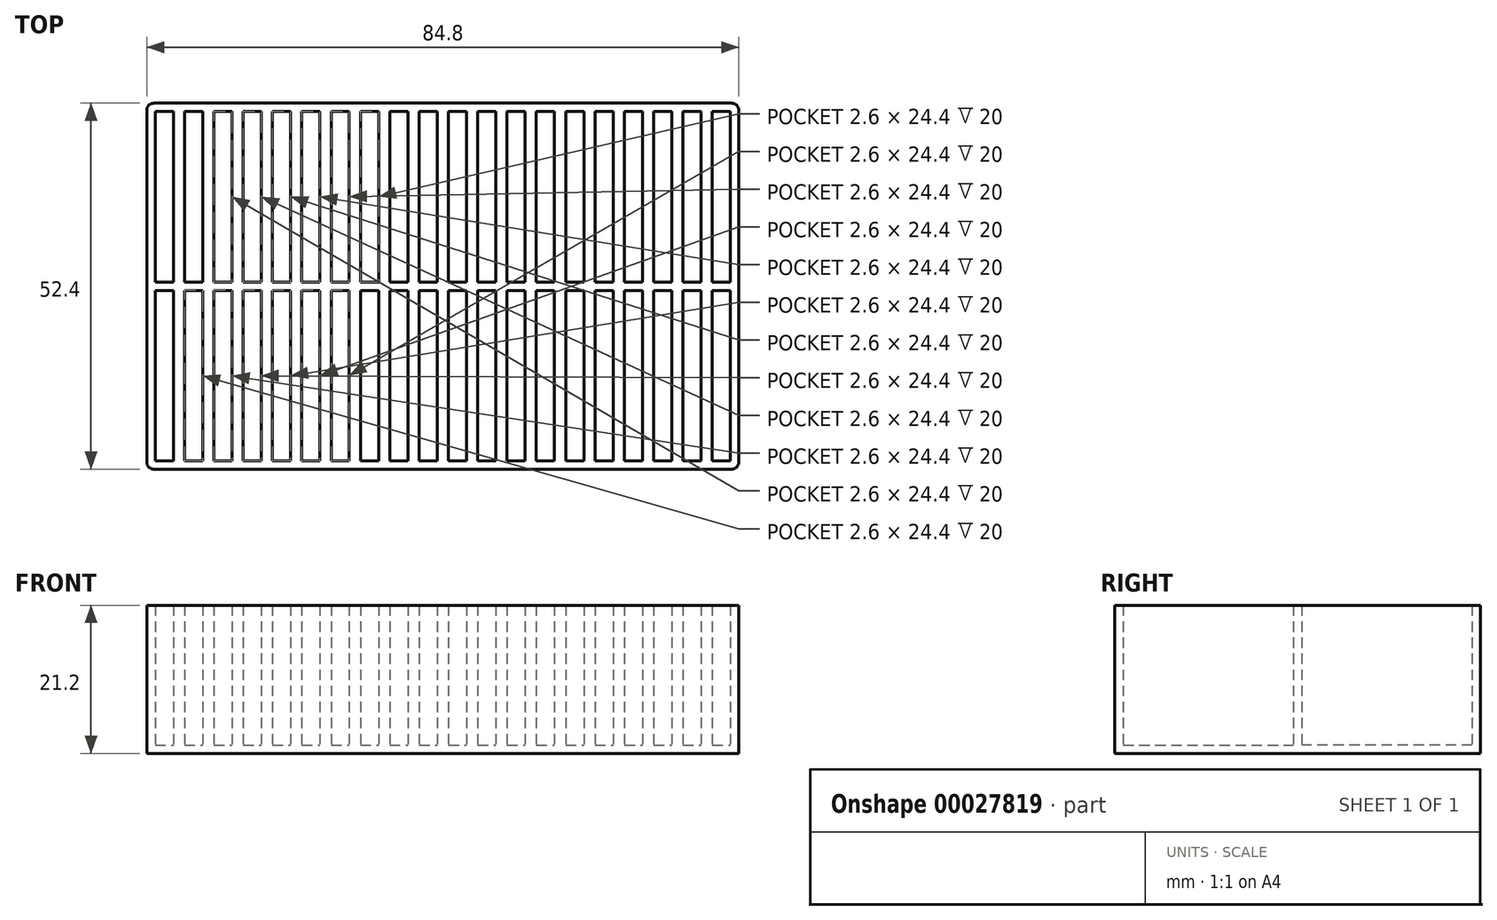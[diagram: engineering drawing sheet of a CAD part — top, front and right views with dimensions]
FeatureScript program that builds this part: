
annotation { "Feature Type Name" : "Feature", "Feature Type Description" : "" }
export const myFeature = defineFeature(function(context is Context, id is Id, definition is map)
    precondition{}
    {
        {
            var Q0;
            Q0=qCreatedBy(makeId("Top.planeOp"),FACE);
            var sketch = newSketch(context, id + "F0", { "sketchPlane" : qUnion([Q0])});
            skLineSegment(sketch, "E0.rect.bottom", {"start": v(-42.4, -26.2) * mm, "end": v(42.4, -26.2) * mm});
            skLineSegment(sketch, "E0.rect.top", {"start": v(-42.4, 26.2) * mm, "end": v(42.4, 26.2) * mm});
            skLineSegment(sketch, "E0.rect.left", {"start": v(-42.4, -26.2) * mm, "end": v(-42.4, 26.2) * mm});
            skLineSegment(sketch, "E0.rect.right", {"start": v(42.4, -26.2) * mm, "end": v(42.4, 26.2) * mm});
            skPoint(sketch, "E0.rect.middle", {"position": v(0, 0) * mm});
            skLineSegment(sketch, "E1", {"start": v(-42.4, 0) * mm, "end": v(42.4, 0) * mm, "construction": true});
            skLineSegment(sketch, "E2.bottom", {"start": v(-41.2, 25) * mm, "end": v(-38.6, 25) * mm});
            skLineSegment(sketch, "E2.top", {"start": v(-41.2, 0.6) * mm, "end": v(-38.6, 0.6) * mm});
            skLineSegment(sketch, "E2.left", {"start": v(-41.2, 25) * mm, "end": v(-41.2, 0.6) * mm});
            skLineSegment(sketch, "E2.right", {"start": v(-38.6, 25) * mm, "end": v(-38.6, 0.6) * mm});
            skLineSegment(sketch, "E3.0.MirrorCS", {"start": v(-38.6, -25) * mm, "end": v(-38.6, -0.6) * mm});
            skLineSegment(sketch, "E4.0.MirrorCS", {"start": v(-41.2, -0.6) * mm, "end": v(-38.6, -0.6) * mm});
            skLineSegment(sketch, "E5.0.MirrorCS", {"start": v(-41.2, -25) * mm, "end": v(-41.2, -0.6) * mm});
            skLineSegment(sketch, "E6.0.MirrorCS", {"start": v(-41.2, -25) * mm, "end": v(-38.6, -25) * mm});
            skLineSegment(sketch, "E7.1.0.0", {"start": v(-37, 25) * mm, "end": v(-37, 0.6) * mm});
            skLineSegment(sketch, "E7.1.0.1", {"start": v(-34.4, 25) * mm, "end": v(-34.4, 0.6) * mm});
            skLineSegment(sketch, "E7.1.0.2", {"start": v(-37, 25) * mm, "end": v(-34.4, 25) * mm});
            skLineSegment(sketch, "E7.1.0.3", {"start": v(-37, 0.6) * mm, "end": v(-34.4, 0.6) * mm});
            skLineSegment(sketch, "E7.1.0.4", {"start": v(-37, -0.6) * mm, "end": v(-34.4, -0.6) * mm});
            skLineSegment(sketch, "E7.1.0.5", {"start": v(-34.4, -25) * mm, "end": v(-34.4, -0.6) * mm});
            skLineSegment(sketch, "E7.1.0.6", {"start": v(-37, -25) * mm, "end": v(-34.4, -25) * mm});
            skLineSegment(sketch, "E7.1.0.7", {"start": v(-37, -25) * mm, "end": v(-37, -0.6) * mm});
            skLineSegment(sketch, "E7.2.0.0", {"start": v(-32.8, 25) * mm, "end": v(-32.8, 0.6) * mm});
            skLineSegment(sketch, "E7.2.0.1", {"start": v(-30.2, 25) * mm, "end": v(-30.2, 0.6) * mm});
            skLineSegment(sketch, "E7.2.0.2", {"start": v(-32.8, 25) * mm, "end": v(-30.2, 25) * mm});
            skLineSegment(sketch, "E7.2.0.3", {"start": v(-32.8, 0.6) * mm, "end": v(-30.2, 0.6) * mm});
            skLineSegment(sketch, "E7.2.0.4", {"start": v(-32.8, -0.6) * mm, "end": v(-30.2, -0.6) * mm});
            skLineSegment(sketch, "E7.2.0.5", {"start": v(-30.2, -25) * mm, "end": v(-30.2, -0.6) * mm});
            skLineSegment(sketch, "E7.2.0.6", {"start": v(-32.8, -25) * mm, "end": v(-30.2, -25) * mm});
            skLineSegment(sketch, "E7.2.0.7", {"start": v(-32.8, -25) * mm, "end": v(-32.8, -0.6) * mm});
            skLineSegment(sketch, "E7.3.0.0", {"start": v(-28.6, 25) * mm, "end": v(-28.6, 0.6) * mm});
            skLineSegment(sketch, "E7.3.0.1", {"start": v(-26, 25) * mm, "end": v(-26, 0.6) * mm});
            skLineSegment(sketch, "E7.3.0.2", {"start": v(-28.6, 25) * mm, "end": v(-26, 25) * mm});
            skLineSegment(sketch, "E7.3.0.3", {"start": v(-28.6, 0.6) * mm, "end": v(-26, 0.6) * mm});
            skLineSegment(sketch, "E7.3.0.4", {"start": v(-28.6, -0.6) * mm, "end": v(-26, -0.6) * mm});
            skLineSegment(sketch, "E7.3.0.5", {"start": v(-26, -25) * mm, "end": v(-26, -0.6) * mm});
            skLineSegment(sketch, "E7.3.0.6", {"start": v(-28.6, -25) * mm, "end": v(-26, -25) * mm});
            skLineSegment(sketch, "E7.3.0.7", {"start": v(-28.6, -25) * mm, "end": v(-28.6, -0.6) * mm});
            skLineSegment(sketch, "E7.4.0.0", {"start": v(-24.4, 25) * mm, "end": v(-24.4, 0.6) * mm});
            skLineSegment(sketch, "E7.4.0.1", {"start": v(-21.8, 25) * mm, "end": v(-21.8, 0.6) * mm});
            skLineSegment(sketch, "E7.4.0.2", {"start": v(-24.4, 25) * mm, "end": v(-21.8, 25) * mm});
            skLineSegment(sketch, "E7.4.0.3", {"start": v(-24.4, 0.6) * mm, "end": v(-21.8, 0.6) * mm});
            skLineSegment(sketch, "E7.4.0.4", {"start": v(-24.4, -0.6) * mm, "end": v(-21.8, -0.6) * mm});
            skLineSegment(sketch, "E7.4.0.5", {"start": v(-21.8, -25) * mm, "end": v(-21.8, -0.6) * mm});
            skLineSegment(sketch, "E7.4.0.6", {"start": v(-24.4, -25) * mm, "end": v(-21.8, -25) * mm});
            skLineSegment(sketch, "E7.4.0.7", {"start": v(-24.4, -25) * mm, "end": v(-24.4, -0.6) * mm});
            skLineSegment(sketch, "E7.5.0.0", {"start": v(-20.2, 25) * mm, "end": v(-20.2, 0.6) * mm});
            skLineSegment(sketch, "E7.5.0.1", {"start": v(-17.6, 25) * mm, "end": v(-17.6, 0.6) * mm});
            skLineSegment(sketch, "E7.5.0.2", {"start": v(-20.2, 25) * mm, "end": v(-17.6, 25) * mm});
            skLineSegment(sketch, "E7.5.0.3", {"start": v(-20.2, 0.6) * mm, "end": v(-17.6, 0.6) * mm});
            skLineSegment(sketch, "E7.5.0.4", {"start": v(-20.2, -0.6) * mm, "end": v(-17.6, -0.6) * mm});
            skLineSegment(sketch, "E7.5.0.5", {"start": v(-17.6, -25) * mm, "end": v(-17.6, -0.6) * mm});
            skLineSegment(sketch, "E7.5.0.6", {"start": v(-20.2, -25) * mm, "end": v(-17.6, -25) * mm});
            skLineSegment(sketch, "E7.5.0.7", {"start": v(-20.2, -25) * mm, "end": v(-20.2, -0.6) * mm});
            skLineSegment(sketch, "E7.6.0.0", {"start": v(-16, 25) * mm, "end": v(-16, 0.6) * mm});
            skLineSegment(sketch, "E7.6.0.1", {"start": v(-13.4, 25) * mm, "end": v(-13.4, 0.6) * mm});
            skLineSegment(sketch, "E7.6.0.2", {"start": v(-16, 25) * mm, "end": v(-13.4, 25) * mm});
            skLineSegment(sketch, "E7.6.0.3", {"start": v(-16, 0.6) * mm, "end": v(-13.4, 0.6) * mm});
            skLineSegment(sketch, "E7.6.0.4", {"start": v(-16, -0.6) * mm, "end": v(-13.4, -0.6) * mm});
            skLineSegment(sketch, "E7.6.0.5", {"start": v(-13.4, -25) * mm, "end": v(-13.4, -0.6) * mm});
            skLineSegment(sketch, "E7.6.0.6", {"start": v(-16, -25) * mm, "end": v(-13.4, -25) * mm});
            skLineSegment(sketch, "E7.6.0.7", {"start": v(-16, -25) * mm, "end": v(-16, -0.6) * mm});
            skLineSegment(sketch, "E7.7.0.0", {"start": v(-11.8, 25) * mm, "end": v(-11.8, 0.6) * mm});
            skLineSegment(sketch, "E7.7.0.1", {"start": v(-9.2, 25) * mm, "end": v(-9.2, 0.6) * mm});
            skLineSegment(sketch, "E7.7.0.2", {"start": v(-11.8, 25) * mm, "end": v(-9.2, 25) * mm});
            skLineSegment(sketch, "E7.7.0.3", {"start": v(-11.8, 0.6) * mm, "end": v(-9.2, 0.6) * mm});
            skLineSegment(sketch, "E7.7.0.4", {"start": v(-11.8, -0.6) * mm, "end": v(-9.2, -0.6) * mm});
            skLineSegment(sketch, "E7.7.0.5", {"start": v(-9.2, -25) * mm, "end": v(-9.2, -0.6) * mm});
            skLineSegment(sketch, "E7.7.0.6", {"start": v(-11.8, -25) * mm, "end": v(-9.2, -25) * mm});
            skLineSegment(sketch, "E7.7.0.7", {"start": v(-11.8, -25) * mm, "end": v(-11.8, -0.6) * mm});
            skLineSegment(sketch, "E7.8.0.0", {"start": v(-7.6, 25) * mm, "end": v(-7.6, 0.6) * mm});
            skLineSegment(sketch, "E7.8.0.1", {"start": v(-5, 25) * mm, "end": v(-5, 0.6) * mm});
            skLineSegment(sketch, "E7.8.0.2", {"start": v(-7.6, 25) * mm, "end": v(-5, 25) * mm});
            skLineSegment(sketch, "E7.8.0.3", {"start": v(-7.6, 0.6) * mm, "end": v(-5, 0.6) * mm});
            skLineSegment(sketch, "E7.8.0.4", {"start": v(-7.6, -0.6) * mm, "end": v(-5, -0.6) * mm});
            skLineSegment(sketch, "E7.8.0.5", {"start": v(-5, -25) * mm, "end": v(-5, -0.6) * mm});
            skLineSegment(sketch, "E7.8.0.6", {"start": v(-7.6, -25) * mm, "end": v(-5, -25) * mm});
            skLineSegment(sketch, "E7.8.0.7", {"start": v(-7.6, -25) * mm, "end": v(-7.6, -0.6) * mm});
            skLineSegment(sketch, "E7.9.0.0", {"start": v(-3.4, 25) * mm, "end": v(-3.4, 0.6) * mm});
            skLineSegment(sketch, "E7.9.0.1", {"start": v(-0.8, 25) * mm, "end": v(-0.8, 0.6) * mm});
            skLineSegment(sketch, "E7.9.0.2", {"start": v(-3.4, 25) * mm, "end": v(-0.8, 25) * mm});
            skLineSegment(sketch, "E7.9.0.3", {"start": v(-3.4, 0.6) * mm, "end": v(-0.8, 0.6) * mm});
            skLineSegment(sketch, "E7.9.0.4", {"start": v(-3.4, -0.6) * mm, "end": v(-0.8, -0.6) * mm});
            skLineSegment(sketch, "E7.9.0.5", {"start": v(-0.8, -25) * mm, "end": v(-0.8, -0.6) * mm});
            skLineSegment(sketch, "E7.9.0.6", {"start": v(-3.4, -25) * mm, "end": v(-0.8, -25) * mm});
            skLineSegment(sketch, "E7.9.0.7", {"start": v(-3.4, -25) * mm, "end": v(-3.4, -0.6) * mm});
            skLineSegment(sketch, "E7.10.0.0", {"start": v(0.8, 25) * mm, "end": v(0.8, 0.6) * mm});
            skLineSegment(sketch, "E7.10.0.1", {"start": v(3.4, 25) * mm, "end": v(3.4, 0.6) * mm});
            skLineSegment(sketch, "E7.10.0.2", {"start": v(0.8, 25) * mm, "end": v(3.4, 25) * mm});
            skLineSegment(sketch, "E7.10.0.3", {"start": v(0.8, 0.6) * mm, "end": v(3.4, 0.6) * mm});
            skLineSegment(sketch, "E7.10.0.4", {"start": v(0.8, -0.6) * mm, "end": v(3.4, -0.6) * mm});
            skLineSegment(sketch, "E7.10.0.5", {"start": v(3.4, -25) * mm, "end": v(3.4, -0.6) * mm});
            skLineSegment(sketch, "E7.10.0.6", {"start": v(0.8, -25) * mm, "end": v(3.4, -25) * mm});
            skLineSegment(sketch, "E7.10.0.7", {"start": v(0.8, -25) * mm, "end": v(0.8, -0.6) * mm});
            skLineSegment(sketch, "E7.11.0.0", {"start": v(5, 25) * mm, "end": v(5, 0.6) * mm});
            skLineSegment(sketch, "E7.11.0.1", {"start": v(7.6, 25) * mm, "end": v(7.6, 0.6) * mm});
            skLineSegment(sketch, "E7.11.0.2", {"start": v(5, 25) * mm, "end": v(7.6, 25) * mm});
            skLineSegment(sketch, "E7.11.0.3", {"start": v(5, 0.6) * mm, "end": v(7.6, 0.6) * mm});
            skLineSegment(sketch, "E7.11.0.4", {"start": v(5, -0.6) * mm, "end": v(7.6, -0.6) * mm});
            skLineSegment(sketch, "E7.11.0.5", {"start": v(7.6, -25) * mm, "end": v(7.6, -0.6) * mm});
            skLineSegment(sketch, "E7.11.0.6", {"start": v(5, -25) * mm, "end": v(7.6, -25) * mm});
            skLineSegment(sketch, "E7.11.0.7", {"start": v(5, -25) * mm, "end": v(5, -0.6) * mm});
            skLineSegment(sketch, "E7.12.0.0", {"start": v(9.2, 25) * mm, "end": v(9.2, 0.6) * mm});
            skLineSegment(sketch, "E7.12.0.1", {"start": v(11.8, 25) * mm, "end": v(11.8, 0.6) * mm});
            skLineSegment(sketch, "E7.12.0.2", {"start": v(9.2, 25) * mm, "end": v(11.8, 25) * mm});
            skLineSegment(sketch, "E7.12.0.3", {"start": v(9.2, 0.6) * mm, "end": v(11.8, 0.6) * mm});
            skLineSegment(sketch, "E7.12.0.4", {"start": v(9.2, -0.6) * mm, "end": v(11.8, -0.6) * mm});
            skLineSegment(sketch, "E7.12.0.5", {"start": v(11.8, -25) * mm, "end": v(11.8, -0.6) * mm});
            skLineSegment(sketch, "E7.12.0.6", {"start": v(9.2, -25) * mm, "end": v(11.8, -25) * mm});
            skLineSegment(sketch, "E7.12.0.7", {"start": v(9.2, -25) * mm, "end": v(9.2, -0.6) * mm});
            skLineSegment(sketch, "E7.13.0.0", {"start": v(13.4, 25) * mm, "end": v(13.4, 0.6) * mm});
            skLineSegment(sketch, "E7.13.0.1", {"start": v(16, 25) * mm, "end": v(16, 0.6) * mm});
            skLineSegment(sketch, "E7.13.0.2", {"start": v(13.4, 25) * mm, "end": v(16, 25) * mm});
            skLineSegment(sketch, "E7.13.0.3", {"start": v(13.4, 0.6) * mm, "end": v(16, 0.6) * mm});
            skLineSegment(sketch, "E7.13.0.4", {"start": v(13.4, -0.6) * mm, "end": v(16, -0.6) * mm});
            skLineSegment(sketch, "E7.13.0.5", {"start": v(16, -25) * mm, "end": v(16, -0.6) * mm});
            skLineSegment(sketch, "E7.13.0.6", {"start": v(13.4, -25) * mm, "end": v(16, -25) * mm});
            skLineSegment(sketch, "E7.13.0.7", {"start": v(13.4, -25) * mm, "end": v(13.4, -0.6) * mm});
            skLineSegment(sketch, "E7.14.0.0", {"start": v(17.6, 25) * mm, "end": v(17.6, 0.6) * mm});
            skLineSegment(sketch, "E7.14.0.1", {"start": v(20.2, 25) * mm, "end": v(20.2, 0.6) * mm});
            skLineSegment(sketch, "E7.14.0.2", {"start": v(17.6, 25) * mm, "end": v(20.2, 25) * mm});
            skLineSegment(sketch, "E7.14.0.3", {"start": v(17.6, 0.6) * mm, "end": v(20.2, 0.6) * mm});
            skLineSegment(sketch, "E7.14.0.4", {"start": v(17.6, -0.6) * mm, "end": v(20.2, -0.6) * mm});
            skLineSegment(sketch, "E7.14.0.5", {"start": v(20.2, -25) * mm, "end": v(20.2, -0.6) * mm});
            skLineSegment(sketch, "E7.14.0.6", {"start": v(17.6, -25) * mm, "end": v(20.2, -25) * mm});
            skLineSegment(sketch, "E7.14.0.7", {"start": v(17.6, -25) * mm, "end": v(17.6, -0.6) * mm});
            skLineSegment(sketch, "E7.15.0.0", {"start": v(21.8, 25) * mm, "end": v(21.8, 0.6) * mm});
            skLineSegment(sketch, "E7.15.0.1", {"start": v(24.4, 25) * mm, "end": v(24.4, 0.6) * mm});
            skLineSegment(sketch, "E7.15.0.2", {"start": v(21.8, 25) * mm, "end": v(24.4, 25) * mm});
            skLineSegment(sketch, "E7.15.0.3", {"start": v(21.8, 0.6) * mm, "end": v(24.4, 0.6) * mm});
            skLineSegment(sketch, "E7.15.0.4", {"start": v(21.8, -0.6) * mm, "end": v(24.4, -0.6) * mm});
            skLineSegment(sketch, "E7.15.0.5", {"start": v(24.4, -25) * mm, "end": v(24.4, -0.6) * mm});
            skLineSegment(sketch, "E7.15.0.6", {"start": v(21.8, -25) * mm, "end": v(24.4, -25) * mm});
            skLineSegment(sketch, "E7.15.0.7", {"start": v(21.8, -25) * mm, "end": v(21.8, -0.6) * mm});
            skLineSegment(sketch, "E7.16.0.0", {"start": v(26, 25) * mm, "end": v(26, 0.6) * mm});
            skLineSegment(sketch, "E7.16.0.1", {"start": v(28.6, 25) * mm, "end": v(28.6, 0.6) * mm});
            skLineSegment(sketch, "E7.16.0.2", {"start": v(26, 25) * mm, "end": v(28.6, 25) * mm});
            skLineSegment(sketch, "E7.16.0.3", {"start": v(26, 0.6) * mm, "end": v(28.6, 0.6) * mm});
            skLineSegment(sketch, "E7.16.0.4", {"start": v(26, -0.6) * mm, "end": v(28.6, -0.6) * mm});
            skLineSegment(sketch, "E7.16.0.5", {"start": v(28.6, -25) * mm, "end": v(28.6, -0.6) * mm});
            skLineSegment(sketch, "E7.16.0.6", {"start": v(26, -25) * mm, "end": v(28.6, -25) * mm});
            skLineSegment(sketch, "E7.16.0.7", {"start": v(26, -25) * mm, "end": v(26, -0.6) * mm});
            skLineSegment(sketch, "E7.17.0.0", {"start": v(30.2, 25) * mm, "end": v(30.2, 0.6) * mm});
            skLineSegment(sketch, "E7.17.0.1", {"start": v(32.8, 25) * mm, "end": v(32.8, 0.6) * mm});
            skLineSegment(sketch, "E7.17.0.2", {"start": v(30.2, 25) * mm, "end": v(32.8, 25) * mm});
            skLineSegment(sketch, "E7.17.0.3", {"start": v(30.2, 0.6) * mm, "end": v(32.8, 0.6) * mm});
            skLineSegment(sketch, "E7.17.0.4", {"start": v(30.2, -0.6) * mm, "end": v(32.8, -0.6) * mm});
            skLineSegment(sketch, "E7.17.0.5", {"start": v(32.8, -25) * mm, "end": v(32.8, -0.6) * mm});
            skLineSegment(sketch, "E7.17.0.6", {"start": v(30.2, -25) * mm, "end": v(32.8, -25) * mm});
            skLineSegment(sketch, "E7.17.0.7", {"start": v(30.2, -25) * mm, "end": v(30.2, -0.6) * mm});
            skLineSegment(sketch, "E7.18.0.0", {"start": v(34.4, 25) * mm, "end": v(34.4, 0.6) * mm});
            skLineSegment(sketch, "E7.18.0.1", {"start": v(37, 25) * mm, "end": v(37, 0.6) * mm});
            skLineSegment(sketch, "E7.18.0.2", {"start": v(34.4, 25) * mm, "end": v(37, 25) * mm});
            skLineSegment(sketch, "E7.18.0.3", {"start": v(34.4, 0.6) * mm, "end": v(37, 0.6) * mm});
            skLineSegment(sketch, "E7.18.0.4", {"start": v(34.4, -0.6) * mm, "end": v(37, -0.6) * mm});
            skLineSegment(sketch, "E7.18.0.5", {"start": v(37, -25) * mm, "end": v(37, -0.6) * mm});
            skLineSegment(sketch, "E7.18.0.6", {"start": v(34.4, -25) * mm, "end": v(37, -25) * mm});
            skLineSegment(sketch, "E7.18.0.7", {"start": v(34.4, -25) * mm, "end": v(34.4, -0.6) * mm});
            skLineSegment(sketch, "E7.19.0.0", {"start": v(38.6, 25) * mm, "end": v(38.6, 0.6) * mm});
            skLineSegment(sketch, "E7.19.0.1", {"start": v(41.2, 25) * mm, "end": v(41.2, 0.6) * mm});
            skLineSegment(sketch, "E7.19.0.2", {"start": v(38.6, 25) * mm, "end": v(41.2, 25) * mm});
            skLineSegment(sketch, "E7.19.0.3", {"start": v(38.6, 0.6) * mm, "end": v(41.2, 0.6) * mm});
            skLineSegment(sketch, "E7.19.0.4", {"start": v(38.6, -0.6) * mm, "end": v(41.2, -0.6) * mm});
            skLineSegment(sketch, "E7.19.0.5", {"start": v(41.2, -25) * mm, "end": v(41.2, -0.6) * mm});
            skLineSegment(sketch, "E7.19.0.6", {"start": v(38.6, -25) * mm, "end": v(41.2, -25) * mm});
            skLineSegment(sketch, "E7.19.0.7", {"start": v(38.6, -25) * mm, "end": v(38.6, -0.6) * mm});
            skLineSegment(sketch, "E7.direction1", {"start": v(-41.2, 0.6) * mm, "end": v(-37, 0.6) * mm, "construction": true});
            skSolve(sketch);
        }
        {
            var Q0;
            Q0=makeQuery(id+"F0.imprint","IMPRINT",FACE,{"disambiguationData":[TD([[makeQuery(id+"F0.imprint","IMPRINT",EDGE,{"derivedFrom":sQuery(id+"F0.wireOp",EDGE,"E0.rect.bottom")}),1.0]])]});
            extrude(context, id + "F1", {"entities" : qUnion([Q0]), "depth" : 20 * mm});
        }
        {
            var Q0;
            Q0=makeQuery(id+"F1.opExtrude","CAP_FACE",FACE,{"disambiguationData":[OSD([sQuery(id+"F0.wireOp",EDGE,"E0.rect.bottom"),sQuery(id+"F0.wireOp",EDGE,"E0.rect.top"),sQuery(id+"F0.wireOp",EDGE,"E0.rect.left"),sQuery(id+"F0.wireOp",EDGE,"E0.rect.right"),sQuery(id+"F0.wireOp",EDGE,"E2.bottom"),sQuery(id+"F0.wireOp",EDGE,"E2.top"),sQuery(id+"F0.wireOp",EDGE,"E2.left"),sQuery(id+"F0.wireOp",EDGE,"E2.right"),sQuery(id+"F0.wireOp",EDGE,"E3.0.MirrorCS"),sQuery(id+"F0.wireOp",EDGE,"E4.0.MirrorCS"),sQuery(id+"F0.wireOp",EDGE,"E5.0.MirrorCS"),sQuery(id+"F0.wireOp",EDGE,"E6.0.MirrorCS"),sQuery(id+"F0.wireOp",EDGE,"E7.1.0.0"),sQuery(id+"F0.wireOp",EDGE,"E7.1.0.1"),sQuery(id+"F0.wireOp",EDGE,"E7.1.0.2"),sQuery(id+"F0.wireOp",EDGE,"E7.1.0.3"),sQuery(id+"F0.wireOp",EDGE,"E7.1.0.4"),sQuery(id+"F0.wireOp",EDGE,"E7.1.0.5"),sQuery(id+"F0.wireOp",EDGE,"E7.1.0.6"),sQuery(id+"F0.wireOp",EDGE,"E7.1.0.7"),sQuery(id+"F0.wireOp",EDGE,"E7.2.0.0"),sQuery(id+"F0.wireOp",EDGE,"E7.2.0.1"),sQuery(id+"F0.wireOp",EDGE,"E7.2.0.2"),sQuery(id+"F0.wireOp",EDGE,"E7.2.0.3"),sQuery(id+"F0.wireOp",EDGE,"E7.2.0.4"),sQuery(id+"F0.wireOp",EDGE,"E7.2.0.5"),sQuery(id+"F0.wireOp",EDGE,"E7.2.0.6"),sQuery(id+"F0.wireOp",EDGE,"E7.2.0.7"),sQuery(id+"F0.wireOp",EDGE,"E7.3.0.0"),sQuery(id+"F0.wireOp",EDGE,"E7.3.0.1"),sQuery(id+"F0.wireOp",EDGE,"E7.3.0.2"),sQuery(id+"F0.wireOp",EDGE,"E7.3.0.3"),sQuery(id+"F0.wireOp",EDGE,"E7.3.0.4"),sQuery(id+"F0.wireOp",EDGE,"E7.3.0.5"),sQuery(id+"F0.wireOp",EDGE,"E7.3.0.6"),sQuery(id+"F0.wireOp",EDGE,"E7.3.0.7"),sQuery(id+"F0.wireOp",EDGE,"E7.4.0.0"),sQuery(id+"F0.wireOp",EDGE,"E7.4.0.1"),sQuery(id+"F0.wireOp",EDGE,"E7.4.0.2"),sQuery(id+"F0.wireOp",EDGE,"E7.4.0.3"),sQuery(id+"F0.wireOp",EDGE,"E7.4.0.4"),sQuery(id+"F0.wireOp",EDGE,"E7.4.0.5"),sQuery(id+"F0.wireOp",EDGE,"E7.4.0.6"),sQuery(id+"F0.wireOp",EDGE,"E7.4.0.7"),sQuery(id+"F0.wireOp",EDGE,"E7.5.0.0"),sQuery(id+"F0.wireOp",EDGE,"E7.5.0.1"),sQuery(id+"F0.wireOp",EDGE,"E7.5.0.2"),sQuery(id+"F0.wireOp",EDGE,"E7.5.0.3"),sQuery(id+"F0.wireOp",EDGE,"E7.5.0.4"),sQuery(id+"F0.wireOp",EDGE,"E7.5.0.5"),sQuery(id+"F0.wireOp",EDGE,"E7.5.0.6"),sQuery(id+"F0.wireOp",EDGE,"E7.5.0.7"),sQuery(id+"F0.wireOp",EDGE,"E7.6.0.0"),sQuery(id+"F0.wireOp",EDGE,"E7.6.0.1"),sQuery(id+"F0.wireOp",EDGE,"E7.6.0.2"),sQuery(id+"F0.wireOp",EDGE,"E7.6.0.3"),sQuery(id+"F0.wireOp",EDGE,"E7.6.0.4"),sQuery(id+"F0.wireOp",EDGE,"E7.6.0.5"),sQuery(id+"F0.wireOp",EDGE,"E7.6.0.6"),sQuery(id+"F0.wireOp",EDGE,"E7.6.0.7"),sQuery(id+"F0.wireOp",EDGE,"E7.7.0.0"),sQuery(id+"F0.wireOp",EDGE,"E7.7.0.1"),sQuery(id+"F0.wireOp",EDGE,"E7.7.0.2"),sQuery(id+"F0.wireOp",EDGE,"E7.7.0.3"),sQuery(id+"F0.wireOp",EDGE,"E7.7.0.4"),sQuery(id+"F0.wireOp",EDGE,"E7.7.0.5"),sQuery(id+"F0.wireOp",EDGE,"E7.7.0.6"),sQuery(id+"F0.wireOp",EDGE,"E7.7.0.7"),sQuery(id+"F0.wireOp",EDGE,"E7.8.0.0"),sQuery(id+"F0.wireOp",EDGE,"E7.8.0.1"),sQuery(id+"F0.wireOp",EDGE,"E7.8.0.2"),sQuery(id+"F0.wireOp",EDGE,"E7.8.0.3"),sQuery(id+"F0.wireOp",EDGE,"E7.8.0.4"),sQuery(id+"F0.wireOp",EDGE,"E7.8.0.5"),sQuery(id+"F0.wireOp",EDGE,"E7.8.0.6"),sQuery(id+"F0.wireOp",EDGE,"E7.8.0.7"),sQuery(id+"F0.wireOp",EDGE,"E7.9.0.0"),sQuery(id+"F0.wireOp",EDGE,"E7.9.0.1"),sQuery(id+"F0.wireOp",EDGE,"E7.9.0.2"),sQuery(id+"F0.wireOp",EDGE,"E7.9.0.3"),sQuery(id+"F0.wireOp",EDGE,"E7.9.0.4"),sQuery(id+"F0.wireOp",EDGE,"E7.9.0.5"),sQuery(id+"F0.wireOp",EDGE,"E7.9.0.6"),sQuery(id+"F0.wireOp",EDGE,"E7.9.0.7"),sQuery(id+"F0.wireOp",EDGE,"E7.10.0.0"),sQuery(id+"F0.wireOp",EDGE,"E7.10.0.1"),sQuery(id+"F0.wireOp",EDGE,"E7.10.0.2"),sQuery(id+"F0.wireOp",EDGE,"E7.10.0.3"),sQuery(id+"F0.wireOp",EDGE,"E7.10.0.4"),sQuery(id+"F0.wireOp",EDGE,"E7.10.0.5"),sQuery(id+"F0.wireOp",EDGE,"E7.10.0.6"),sQuery(id+"F0.wireOp",EDGE,"E7.10.0.7"),sQuery(id+"F0.wireOp",EDGE,"E7.11.0.0"),sQuery(id+"F0.wireOp",EDGE,"E7.11.0.1"),sQuery(id+"F0.wireOp",EDGE,"E7.11.0.2"),sQuery(id+"F0.wireOp",EDGE,"E7.11.0.3"),sQuery(id+"F0.wireOp",EDGE,"E7.11.0.4"),sQuery(id+"F0.wireOp",EDGE,"E7.11.0.5"),sQuery(id+"F0.wireOp",EDGE,"E7.11.0.6"),sQuery(id+"F0.wireOp",EDGE,"E7.11.0.7"),sQuery(id+"F0.wireOp",EDGE,"E7.12.0.0"),sQuery(id+"F0.wireOp",EDGE,"E7.12.0.1"),sQuery(id+"F0.wireOp",EDGE,"E7.12.0.2"),sQuery(id+"F0.wireOp",EDGE,"E7.12.0.3"),sQuery(id+"F0.wireOp",EDGE,"E7.12.0.4"),sQuery(id+"F0.wireOp",EDGE,"E7.12.0.5"),sQuery(id+"F0.wireOp",EDGE,"E7.12.0.6"),sQuery(id+"F0.wireOp",EDGE,"E7.12.0.7"),sQuery(id+"F0.wireOp",EDGE,"E7.13.0.0"),sQuery(id+"F0.wireOp",EDGE,"E7.13.0.1"),sQuery(id+"F0.wireOp",EDGE,"E7.13.0.2"),sQuery(id+"F0.wireOp",EDGE,"E7.13.0.3"),sQuery(id+"F0.wireOp",EDGE,"E7.13.0.4"),sQuery(id+"F0.wireOp",EDGE,"E7.13.0.5"),sQuery(id+"F0.wireOp",EDGE,"E7.13.0.6"),sQuery(id+"F0.wireOp",EDGE,"E7.13.0.7"),sQuery(id+"F0.wireOp",EDGE,"E7.14.0.0"),sQuery(id+"F0.wireOp",EDGE,"E7.14.0.1"),sQuery(id+"F0.wireOp",EDGE,"E7.14.0.2"),sQuery(id+"F0.wireOp",EDGE,"E7.14.0.3"),sQuery(id+"F0.wireOp",EDGE,"E7.14.0.4"),sQuery(id+"F0.wireOp",EDGE,"E7.14.0.5"),sQuery(id+"F0.wireOp",EDGE,"E7.14.0.6"),sQuery(id+"F0.wireOp",EDGE,"E7.14.0.7"),sQuery(id+"F0.wireOp",EDGE,"E7.15.0.0"),sQuery(id+"F0.wireOp",EDGE,"E7.15.0.1"),sQuery(id+"F0.wireOp",EDGE,"E7.15.0.2"),sQuery(id+"F0.wireOp",EDGE,"E7.15.0.3"),sQuery(id+"F0.wireOp",EDGE,"E7.15.0.4"),sQuery(id+"F0.wireOp",EDGE,"E7.15.0.5"),sQuery(id+"F0.wireOp",EDGE,"E7.15.0.6"),sQuery(id+"F0.wireOp",EDGE,"E7.15.0.7"),sQuery(id+"F0.wireOp",EDGE,"E7.16.0.0"),sQuery(id+"F0.wireOp",EDGE,"E7.16.0.1"),sQuery(id+"F0.wireOp",EDGE,"E7.16.0.2"),sQuery(id+"F0.wireOp",EDGE,"E7.16.0.3"),sQuery(id+"F0.wireOp",EDGE,"E7.16.0.4"),sQuery(id+"F0.wireOp",EDGE,"E7.16.0.5"),sQuery(id+"F0.wireOp",EDGE,"E7.16.0.6"),sQuery(id+"F0.wireOp",EDGE,"E7.16.0.7"),sQuery(id+"F0.wireOp",EDGE,"E7.17.0.0"),sQuery(id+"F0.wireOp",EDGE,"E7.17.0.1"),sQuery(id+"F0.wireOp",EDGE,"E7.17.0.2"),sQuery(id+"F0.wireOp",EDGE,"E7.17.0.3"),sQuery(id+"F0.wireOp",EDGE,"E7.17.0.4"),sQuery(id+"F0.wireOp",EDGE,"E7.17.0.5"),sQuery(id+"F0.wireOp",EDGE,"E7.17.0.6"),sQuery(id+"F0.wireOp",EDGE,"E7.17.0.7"),sQuery(id+"F0.wireOp",EDGE,"E7.18.0.0"),sQuery(id+"F0.wireOp",EDGE,"E7.18.0.1"),sQuery(id+"F0.wireOp",EDGE,"E7.18.0.2"),sQuery(id+"F0.wireOp",EDGE,"E7.18.0.3"),sQuery(id+"F0.wireOp",EDGE,"E7.18.0.4"),sQuery(id+"F0.wireOp",EDGE,"E7.18.0.5"),sQuery(id+"F0.wireOp",EDGE,"E7.18.0.6"),sQuery(id+"F0.wireOp",EDGE,"E7.18.0.7"),sQuery(id+"F0.wireOp",EDGE,"E7.19.0.0"),sQuery(id+"F0.wireOp",EDGE,"E7.19.0.1"),sQuery(id+"F0.wireOp",EDGE,"E7.19.0.2"),sQuery(id+"F0.wireOp",EDGE,"E7.19.0.3"),sQuery(id+"F0.wireOp",EDGE,"E7.19.0.4"),sQuery(id+"F0.wireOp",EDGE,"E7.19.0.5"),sQuery(id+"F0.wireOp",EDGE,"E7.19.0.6"),sQuery(id+"F0.wireOp",EDGE,"E7.19.0.7")])],"isStart":true});
            var sketch = newSketch(context, id + "F2", { "sketchPlane" : qUnion([Q0])});
            skLineSegment(sketch, "E8.bottom", {"start": v(-42.4, 26.2) * mm, "end": v(42.4, 26.2) * mm});
            skLineSegment(sketch, "E8.top", {"start": v(-42.4, -26.2) * mm, "end": v(42.4, -26.2) * mm});
            skLineSegment(sketch, "E8.left", {"start": v(-42.4, 26.2) * mm, "end": v(-42.4, -26.2) * mm});
            skLineSegment(sketch, "E8.right", {"start": v(42.4, 26.2) * mm, "end": v(42.4, -26.2) * mm});
            skSolve(sketch);
        }
        {
            var Q0;
            Q0=qSketchRegion(id+"F2",true);
            extrude(context, id + "F3", {"entities" : qUnion([Q0]), "operationType" : NewBodyOperationType.ADD, "depth" : 1.2 * mm});
        }
        {
            var Q0;
            Q0=makeQuery(id+"F3.boolean.opBoolean","MERGE",EDGE,{"derivedFrom":[makeQuery(id+"F1.opExtrude","SWEPT_EDGE",EDGE,{"disambiguationData":[OSD([sQuery(id+"F0.wireOp",EDGE,"E0.rect.bottom"),sQuery(id+"F0.wireOp",EDGE,"E0.rect.left")])]}),makeQuery(id+"F3.opExtrude","SWEPT_EDGE",EDGE,{"disambiguationData":[OSD([sQuery(id+"F2.wireOp",EDGE,"E8.bottom"),sQuery(id+"F2.wireOp",EDGE,"E8.left")])]})]});
            var Q1;
            Q1=makeQuery(id+"F3.boolean.opBoolean","MERGE",EDGE,{"derivedFrom":[makeQuery(id+"F1.opExtrude","SWEPT_EDGE",EDGE,{"disambiguationData":[OSD([sQuery(id+"F0.wireOp",EDGE,"E0.rect.top"),sQuery(id+"F0.wireOp",EDGE,"E0.rect.left")])]}),makeQuery(id+"F3.opExtrude","SWEPT_EDGE",EDGE,{"disambiguationData":[OSD([sQuery(id+"F2.wireOp",EDGE,"E8.top"),sQuery(id+"F2.wireOp",EDGE,"E8.left")])]})]});
            var Q2;
            Q2=makeQuery(id+"F3.boolean.opBoolean","MERGE",EDGE,{"derivedFrom":[makeQuery(id+"F1.opExtrude","SWEPT_EDGE",EDGE,{"disambiguationData":[OSD([sQuery(id+"F0.wireOp",EDGE,"E0.rect.bottom"),sQuery(id+"F0.wireOp",EDGE,"E0.rect.right")])]}),makeQuery(id+"F3.opExtrude","SWEPT_EDGE",EDGE,{"disambiguationData":[OSD([sQuery(id+"F2.wireOp",EDGE,"E8.bottom"),sQuery(id+"F2.wireOp",EDGE,"E8.right")])]})]});
            var Q3;
            Q3=makeQuery(id+"F3.boolean.opBoolean","MERGE",EDGE,{"derivedFrom":[makeQuery(id+"F1.opExtrude","SWEPT_EDGE",EDGE,{"disambiguationData":[OSD([sQuery(id+"F0.wireOp",EDGE,"E0.rect.top"),sQuery(id+"F0.wireOp",EDGE,"E0.rect.right")])]}),makeQuery(id+"F3.opExtrude","SWEPT_EDGE",EDGE,{"disambiguationData":[OSD([sQuery(id+"F2.wireOp",EDGE,"E8.top"),sQuery(id+"F2.wireOp",EDGE,"E8.right")])]})]});
            fillet(context, id + "F4", {"entities" : qUnion([Q0, Q1, Q2, Q3]), "radius" : 1 * mm, "tangentPropagation" : true, "allowEdgeOverflow" : false});
        }
    });
